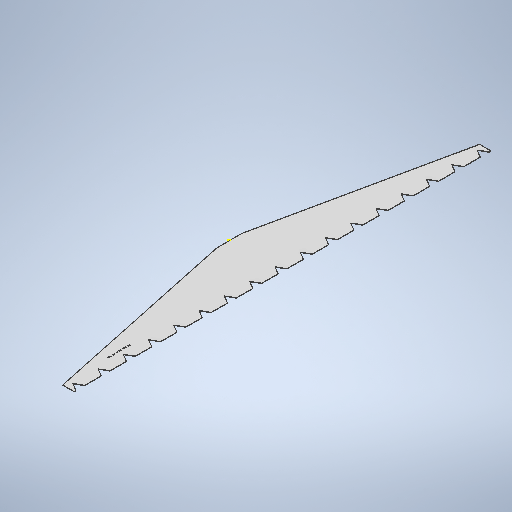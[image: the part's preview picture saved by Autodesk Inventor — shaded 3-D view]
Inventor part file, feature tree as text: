
AUTODESK INVENTOR PART (.ipt)
format: ipt  version: 2025 (Build 290162010, 162A)  size: 470,016 bytes
history: native  units: mm
features: sketch x4, other x4, sheet_metal_op x1, pattern_linear x1, projected_geometry x1
ambient origin geometry x8: Origin, YZ Plane, XZ Plane, XY Plane, X Axis, Y Axis, Z Axis, Center Point
bodies: Solid1 (feature_tree)
feature tree (11):
  sheet_metal_op  "Face1"
  sketch  "Sketch8"  dims[d26=500.0mm]
  other  "Mark1"
  pattern_linear  "Rectangular Pattern2"  Count1=42  [1 undecoded]
  sketch  "Sketch1"  dims[d1=3300.0mm]
  other  "Plate1"
  sketch  "Sketch5"  dims[d2=3.0mm]
  projected_geometry  "Projected Loop1"
  sketch  "Sketch9"  dims[d27=8.37758mm d28=672.816365mm d31=3.0mm d32=0.0mm d36=200.0mm d37=15.0mm d41=200.0mm d42=90.0mm d44=60.0mm d45=180.0mm d47=200.0mm d48=70.0mm]
  other  "Cut1"
  other  "Definition1"
note: 1 required parameter value undecoded (feature->parameter linkage not recoverable at this tier; creation-order binding heuristic only, values carry confidence <= 0.55)
